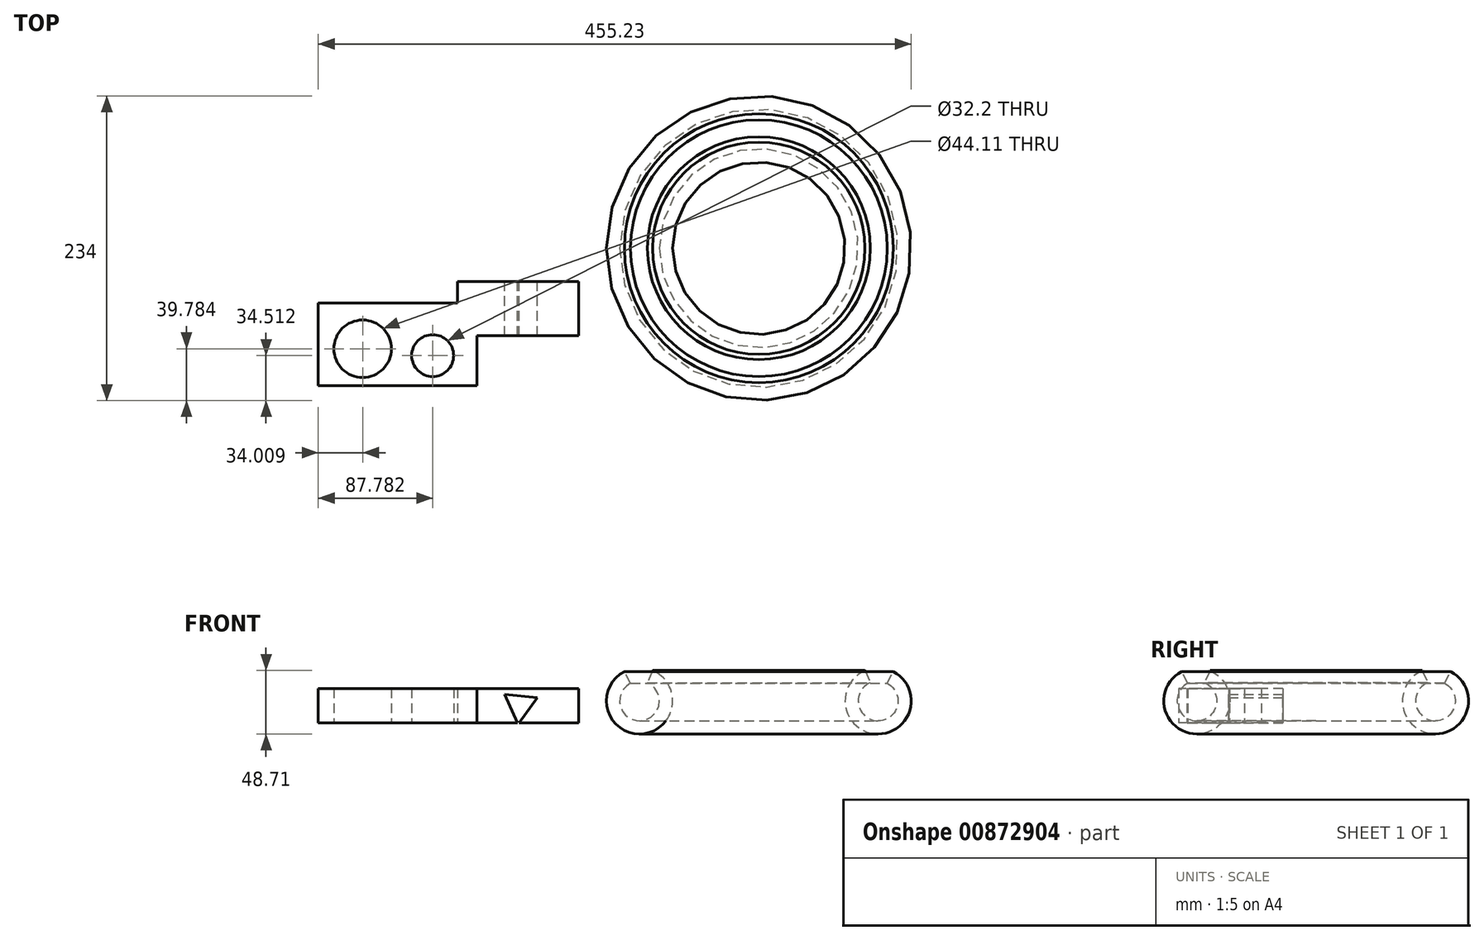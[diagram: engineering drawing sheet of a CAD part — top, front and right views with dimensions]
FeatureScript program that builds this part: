
annotation { "Feature Type Name" : "Feature", "Feature Type Description" : "" }
export const myFeature = defineFeature(function(context is Context, id is Id, definition is map)
    precondition{}
    {
        {
            var Q0;
            Q0=qCreatedBy(makeId("Front.planeOp"),FACE);
            var sketch = newSketch(context, id + "F0", { "sketchPlane" : qUnion([Q0])});
            skLineSegment(sketch, "E0", {"start": v(0, 0) * mm, "end": v(0, 32.85) * mm, "construction": true});
            skCircle(sketch, "E1", {"center": v(91.6, 16.77) * mm, "radius": 25.4 * mm});
            skCircle(sketch, "E2", {"center": v(91.6, 16.77) * mm, "radius": 15.24 * mm});
            skLineSegment(sketch, "E3", {"start": v(-103.83, 10.74) * mm, "end": v(-44.64, -28.33) * mm, "construction": true});
            skLineSegment(sketch, "E4", {"start": v(25.92, -53.4) * mm, "end": v(90.65, -17.54) * mm, "construction": true});
            skSolve(sketch);
        }
        {
            var Q0;
            Q0 = qSketchRegion(id + "F0", true);
            var Q1;
            Q1=sQuery(id+"F0.wireOp",EDGE,"E0");
            revolve(context, id + "F1", {"surfaceOperationType" : NewSurfaceOperationType.NEW, "entities" : qUnion([Q0]), "axis" : qUnion([Q1]), "revolveType" : RevolveType.FULL});
        }
        {
            var Q0;
            Q0=qCreatedBy(makeId("Front.planeOp"),FACE);
            var sketch = newSketch(context, id + "F2", { "sketchPlane" : qUnion([Q0])});
            skLineSegment(sketch, "E5", {"start": v(76.35, 52.02) * mm, "end": v(91.58, 16.79) * mm});
            skLineSegment(sketch, "E6", {"start": v(91.58, 16.79) * mm, "end": v(109.82, 52.02) * mm});
            skLineSegment(sketch, "E7", {"start": v(109.82, 52.02) * mm, "end": v(76.35, 52.02) * mm});
            skSolve(sketch);
        }
        {
            var Q0;
            Q0 = qSketchRegion(id + "F2", true);
            var Q1;
            Q1=sQuery(id+"F0.wireOp",EDGE,"E0");
            revolve(context, id + "F3", {"operationType" : NewBodyOperationType.REMOVE, "surfaceOperationType" : NewSurfaceOperationType.NEW, "entities" : qUnion([Q0]), "axis" : qUnion([Q1]), "revolveType" : RevolveType.FULL, "oppositeDirection" : true});
        }
        {
            var Q0;
            Q0=qCreatedBy(makeId("Top.planeOp"),FACE);
            var sketch = newSketch(context, id + "F4", { "sketchPlane" : qUnion([Q0])});
            skLineSegment(sketch, "E8.bottom", {"start": v(-338.23, -42.2) * mm, "end": v(-231.5, -42.2) * mm});
            skLineSegment(sketch, "E8.top", {"start": v(-338.23, -105.5) * mm, "end": v(-216.41, -105.5) * mm});
            skLineSegment(sketch, "E8.left", {"start": v(-338.23, -42.2) * mm, "end": v(-338.23, -105.5) * mm});
            skLineSegment(sketch, "E8.right", {"start": v(-216.41, -67.25) * mm, "end": v(-216.41, -105.5) * mm});
            skCircle(sketch, "E9", {"center": v(-250.45, -82.49) * mm, "radius": 16.1 * mm});
            skCircle(sketch, "E10", {"center": v(-304.22, -77.22) * mm, "radius": 22.06 * mm});
            skLineSegment(sketch, "E11.bottom", {"start": v(-231.5, -25.43) * mm, "end": v(-138.18, -25.43) * mm});
            skLineSegment(sketch, "E11.top", {"start": v(-216.41, -67.25) * mm, "end": v(-138.18, -67.25) * mm});
            skLineSegment(sketch, "E11.left", {"start": v(-231.5, -25.43) * mm, "end": v(-231.5, -42.2) * mm});
            skLineSegment(sketch, "E11.right", {"start": v(-138.18, -25.43) * mm, "end": v(-138.18, -67.25) * mm});
            skPoint(sketch, "E11.middle", {"position": v(-184.85, -46.34) * mm});
            skPoint(sketch, "E12.orphan", {"position": v(-231.5, -67.25) * mm});
            skSolve(sketch);
        }
        {
            var Q0;
            Q0=makeQuery(id+"F4.imprint","IMPRINT",FACE,{"disambiguationData":[TD([[makeQuery(id+"F4.imprint","IMPRINT",EDGE,{"derivedFrom":sQuery(id+"F4.wireOp",EDGE,"E8.bottom")}),-1.0]])]});
            extrude(context, id + "F5", {"entities" : qUnion([Q0]), "depth" : 26.42 * mm, "offsetDistance" : 25.4 * mm});
        }
        {
            var Q0;
            Q0=makeQuery(id+"F5.opExtrude","SWEPT_FACE",FACE,{"disambiguationData":[OSD([sQuery(id+"F4.wireOp",EDGE,"E11.bottom")])]});
            var sketch = newSketch(context, id + "F6", { "sketchPlane" : qUnion([Q0])});
            skCircle(sketch, "E13.cCircle", {"center": v(183.43, 13.29) * mm, "radius": 7.26 * mm, "construction": true});
            skLineSegment(sketch, "E13.0", {"start": v(195.24, 21.74) * mm, "end": v(184.85, -1.17) * mm});
            skLineSegment(sketch, "E13.1", {"start": v(184.85, -1.17) * mm, "end": v(170.2, 19.29) * mm});
            skLineSegment(sketch, "E13.2", {"start": v(170.2, 19.29) * mm, "end": v(195.24, 21.74) * mm});
            skPoint(sketch, "E13.0.midPoint", {"position": v(190.04, 10.29) * mm});
            skSolve(sketch);
        }
        {
            var Q0;
            {var subQ0=sQuery(id+"F6.wireOp",EDGE,"E13.2");Q0=makeQuery(id+"F6.imprint","IMPRINT",FACE,{"disambiguationData":[TD([[makeQuery(id+"F6.imprint","IMPRINT",EDGE,{"derivedFrom":subQ0}),-1.0]])]});}
            extrude(context, id + "F7", {"entities" : qUnion([Q0]), "operationType" : NewBodyOperationType.REMOVE, "endBound" : BoundingType.THROUGH_ALL, "oppositeDirection" : true, "depth" : 134.37 * mm, "offsetDistance" : 25.4 * mm});
        }
    });
